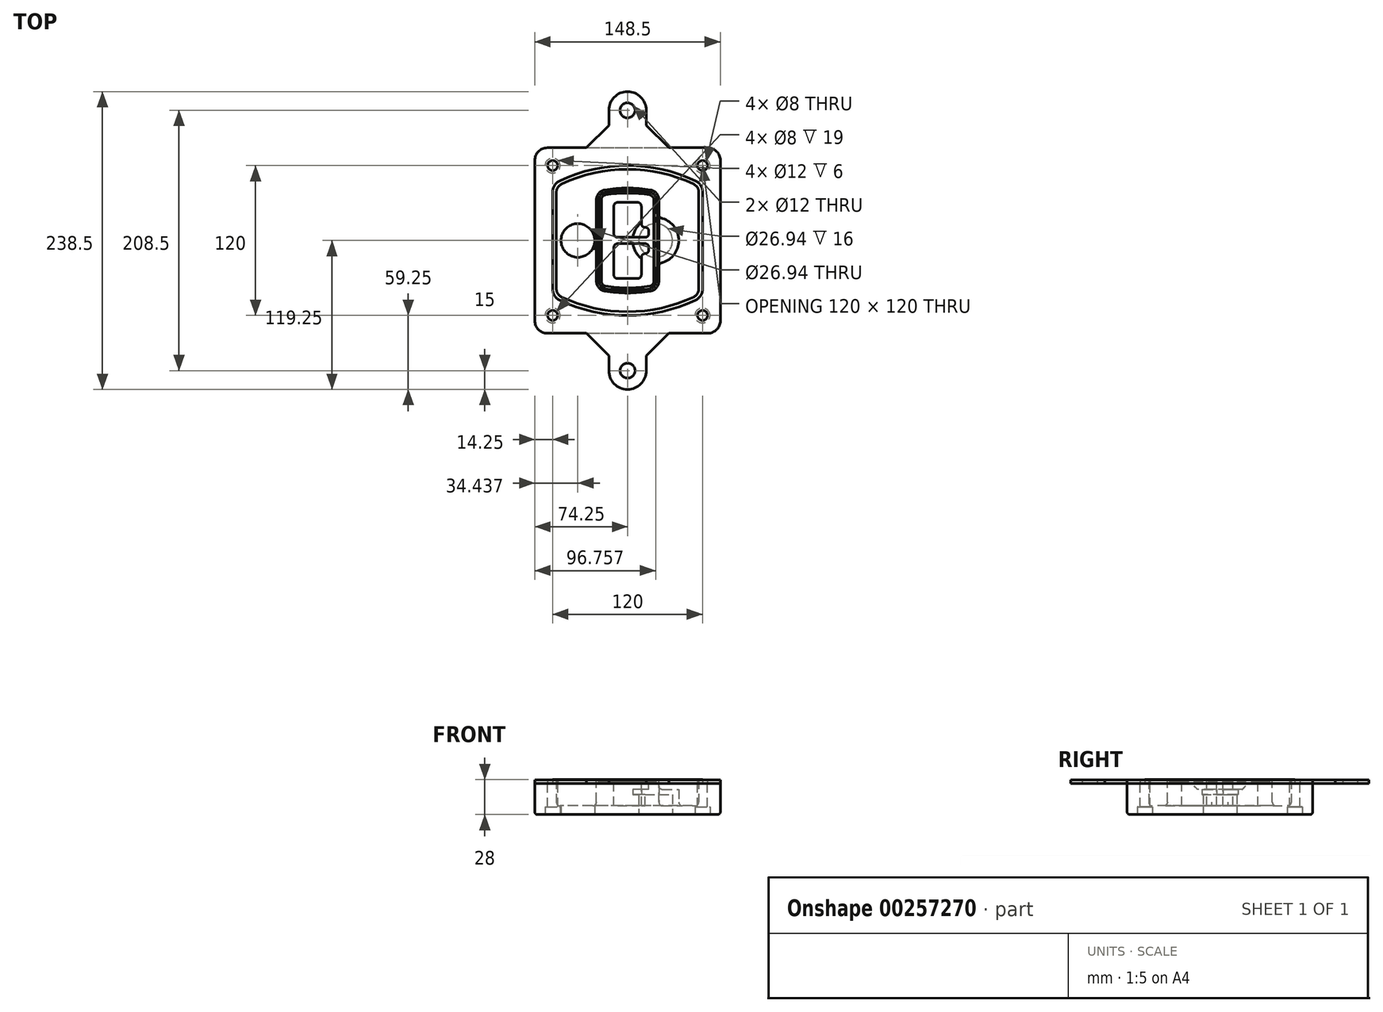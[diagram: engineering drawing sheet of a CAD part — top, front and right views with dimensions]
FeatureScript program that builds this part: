
annotation { "Feature Type Name" : "Feature", "Feature Type Description" : "" }
export const myFeature = defineFeature(function(context is Context, id is Id, definition is map)
    precondition{}
    {
        {
            var Q0;
            Q0=qCreatedBy(makeId("Top.planeOp"),FACE);
            var sketch = newSketch(context, id + "F0", { "sketchPlane" : qUnion([Q0])});
            skPoint(sketch, "E0.rect.middle", {"position": v(0, 0) * mm});
            skLineSegment(sketch, "E1.bottom", {"start": v(-64.25, -74.25) * mm, "end": v(64.25, -74.25) * mm});
            skLineSegment(sketch, "E1.top", {"start": v(-64.25, 74.25) * mm, "end": v(64.25, 74.25) * mm});
            skLineSegment(sketch, "E1.left", {"start": v(-74.25, -64.25) * mm, "end": v(-74.25, 64.25) * mm});
            skLineSegment(sketch, "E1.right", {"start": v(74.25, -64.25) * mm, "end": v(74.25, 64.25) * mm});
            skLineSegment(sketch, "E2", {"start": v(-74.25, 74.25) * mm, "end": v(74.25, -74.25) * mm, "construction": true});
            skLineSegment(sketch, "E3", {"start": v(74.25, 74.25) * mm, "end": v(-74.25, -74.25) * mm, "construction": true});
            skCircle(sketch, "E4", {"center": v(-60, 60) * mm, "radius": 4 * mm});
            skCircle(sketch, "E5", {"center": v(60, 60) * mm, "radius": 4 * mm});
            skCircle(sketch, "E6", {"center": v(60, -60) * mm, "radius": 4 * mm});
            skCircle(sketch, "E7", {"center": v(-60, -60) * mm, "radius": 4 * mm});
            skLineSegment(sketch, "E8", {"start": v(-60, 60) * mm, "end": v(60, 60) * mm, "construction": true});
            skLineSegment(sketch, "E9", {"start": v(60, 60) * mm, "end": v(60, -60) * mm, "construction": true});
            skLineSegment(sketch, "E10", {"start": v(60, -60) * mm, "end": v(-60, -60) * mm, "construction": true});
            skLineSegment(sketch, "E11", {"start": v(-60, -60) * mm, "end": v(-60, 60) * mm, "construction": true});
            skLineSegment(sketch, "E12", {"start": v(-60, 38.83) * mm, "end": v(-60, -38.83) * mm});
            skLineSegment(sketch, "E13", {"start": v(60, 38.83) * mm, "end": v(60, -38.83) * mm});
            skArc(sketch, "E14", {"start": v(54.26, 47.88) * mm, "mid": v(0, 60) * mm, "end": v(-54.26, 47.88) * mm});
            skArc(sketch, "E15", {"start": v(-54.26, -47.88) * mm, "mid": v(0, -60) * mm, "end": v(54.26, -47.88) * mm});
            skLineSegment(sketch, "E16", {"start": v(-60, 0) * mm, "end": v(60, 0) * mm, "construction": true});
            skPoint(sketch, "E17.visualSharp", {"position": v(-60, -45) * mm});
            skArc(sketch, "E17.filletArc", {"start": v(-60, -38.83) * mm, "mid": v(-58.44, -44.2) * mm, "end": v(-54.26, -47.88) * mm});
            skPoint(sketch, "E18.visualSharp", {"position": v(-60, 45) * mm});
            skArc(sketch, "E18.filletArc", {"start": v(-54.26, 47.88) * mm, "mid": v(-58.44, 44.2) * mm, "end": v(-60, 38.83) * mm});
            skPoint(sketch, "E19.visualSharp", {"position": v(60, 45) * mm});
            skArc(sketch, "E19.filletArc", {"start": v(60, 38.83) * mm, "mid": v(58.44, 44.2) * mm, "end": v(54.26, 47.88) * mm});
            skPoint(sketch, "E20.visualSharp", {"position": v(60, -45) * mm});
            skArc(sketch, "E20.filletArc", {"start": v(54.26, -47.88) * mm, "mid": v(58.44, -44.2) * mm, "end": v(60, -38.83) * mm});
            skPoint(sketch, "E21.visualSharp", {"position": v(-74.25, 74.25) * mm});
            skArc(sketch, "E21.filletArc", {"start": v(-64.25, 74.25) * mm, "mid": v(-71.32, 71.32) * mm, "end": v(-74.25, 64.25) * mm});
            skPoint(sketch, "E22.visualSharp", {"position": v(74.25, 74.25) * mm});
            skArc(sketch, "E22.filletArc", {"start": v(74.25, 64.25) * mm, "mid": v(71.32, 71.32) * mm, "end": v(64.25, 74.25) * mm});
            skPoint(sketch, "E23.visualSharp", {"position": v(74.25, -74.25) * mm});
            skArc(sketch, "E23.filletArc", {"start": v(64.25, -74.25) * mm, "mid": v(71.32, -71.32) * mm, "end": v(74.25, -64.25) * mm});
            skPoint(sketch, "E24.visualSharp", {"position": v(-74.25, -74.25) * mm});
            skArc(sketch, "E24.filletArc", {"start": v(-74.25, -64.25) * mm, "mid": v(-71.32, -71.32) * mm, "end": v(-64.25, -74.25) * mm});
            skArc(sketch, "E25.0", {"start": v(57, 38.83) * mm, "mid": v(55.9, 42.58) * mm, "end": v(52.98, 45.17) * mm});
            skLineSegment(sketch, "E25.1", {"start": v(57, 38.83) * mm, "end": v(57, -38.83) * mm});
            skArc(sketch, "E25.2", {"start": v(52.98, -45.17) * mm, "mid": v(55.9, -42.58) * mm, "end": v(57, -38.83) * mm});
            skArc(sketch, "E25.3", {"start": v(-52.98, -45.17) * mm, "mid": v(0, -57) * mm, "end": v(52.98, -45.17) * mm});
            skArc(sketch, "E25.4", {"start": v(-57, -38.83) * mm, "mid": v(-55.9, -42.58) * mm, "end": v(-52.98, -45.17) * mm});
            skArc(sketch, "E25.5", {"start": v(52.98, 45.17) * mm, "mid": v(0, 57) * mm, "end": v(-52.98, 45.17) * mm});
            skLineSegment(sketch, "E25.6", {"start": v(-57, 38.83) * mm, "end": v(-57, -38.83) * mm});
            skArc(sketch, "E25.7", {"start": v(-52.98, 45.17) * mm, "mid": v(-55.9, 42.58) * mm, "end": v(-57, 38.83) * mm});
            skArc(sketch, "E26.0", {"start": v(-55.96, 51.5) * mm, "mid": v(-61.82, 46.33) * mm, "end": v(-64, 38.83) * mm});
            skArc(sketch, "E26.1", {"start": v(55.96, 51.5) * mm, "mid": v(0, 64) * mm, "end": v(-55.96, 51.5) * mm});
            skArc(sketch, "E26.2", {"start": v(64, 38.83) * mm, "mid": v(61.82, 46.33) * mm, "end": v(55.96, 51.5) * mm});
            skLineSegment(sketch, "E26.3", {"start": v(64, 38.83) * mm, "end": v(64, -38.83) * mm});
            skArc(sketch, "E26.4", {"start": v(55.96, -51.5) * mm, "mid": v(61.82, -46.33) * mm, "end": v(64, -38.83) * mm});
            skLineSegment(sketch, "E26.5", {"start": v(-64, 38.83) * mm, "end": v(-64, -38.83) * mm});
            skArc(sketch, "E26.6", {"start": v(-55.96, -51.5) * mm, "mid": v(0, -64) * mm, "end": v(55.96, -51.5) * mm});
            skArc(sketch, "E26.7", {"start": v(-64, -38.83) * mm, "mid": v(-61.82, -46.33) * mm, "end": v(-55.96, -51.5) * mm});
            skSolve(sketch);
        }
        {
            var Q0;
            Q0=makeQuery(id+"F0.imprint","IMPRINT",FACE,{"disambiguationData":[TD([[makeQuery(id+"F0.imprint","IMPRINT",EDGE,{"derivedFrom":sQuery(id+"F0.wireOp",EDGE,"E1.bottom")}),1.0]])]});
            var Q1;
            Q1=makeQuery(id+"F0.imprint","IMPRINT",FACE,{"disambiguationData":[TD([[makeQuery(id+"F0.imprint","IMPRINT",EDGE,{"derivedFrom":sQuery(id+"F0.wireOp",EDGE,"E12")}),1.0]])]});
            var Q2;
            Q2=makeQuery(id+"F0.imprint","IMPRINT",FACE,{"disambiguationData":[TD([[makeQuery(id+"F0.imprint","IMPRINT",EDGE,{"derivedFrom":sQuery(id+"F0.wireOp",EDGE,"E25.0")}),1.0]])]});
            var Q3;
            Q3=makeQuery(id+"F0.imprint","IMPRINT",FACE,{"disambiguationData":[TD([[makeQuery(id+"F0.imprint","IMPRINT",EDGE,{"derivedFrom":sQuery(id+"F0.wireOp",EDGE,"E12")}),-1.0]])]});
            extrude(context, id + "F1", {"entities" : qUnion([Q0, Q1, Q2, Q3]), "oppositeDirection" : true, "depth" : 25 * mm});
        }
        {
            var Q0;
            Q0=makeQuery(id+"F0.imprint","IMPRINT",FACE,{"disambiguationData":[TD([[makeQuery(id+"F0.imprint","IMPRINT",EDGE,{"derivedFrom":sQuery(id+"F0.wireOp",EDGE,"E12")}),1.0]])]});
            extrude(context, id + "F2", {"entities" : qUnion([Q0]), "operationType" : NewBodyOperationType.ADD, "depth" : 3 * mm});
        }
        {
            var Q0;
            Q0=makeQuery(id+"F0.imprint","IMPRINT",FACE,{"disambiguationData":[TD([[makeQuery(id+"F0.imprint","IMPRINT",EDGE,{"derivedFrom":sQuery(id+"F0.wireOp",EDGE,"E25.0")}),1.0]])]});
            extrude(context, id + "F3", {"entities" : qUnion([Q0]), "operationType" : NewBodyOperationType.REMOVE, "oppositeDirection" : true, "depth" : 18 * mm});
        }
        {
            var Q0;
            Q0=makeQuery(id+"F2.opExtrude","CAP_FACE",FACE,{"disambiguationData":[OSD([sQuery(id+"F0.wireOp",EDGE,"E12"),sQuery(id+"F0.wireOp",EDGE,"E13"),sQuery(id+"F0.wireOp",EDGE,"E14"),sQuery(id+"F0.wireOp",EDGE,"E15"),sQuery(id+"F0.wireOp",EDGE,"E17.filletArc"),sQuery(id+"F0.wireOp",EDGE,"E18.filletArc"),sQuery(id+"F0.wireOp",EDGE,"E19.filletArc"),sQuery(id+"F0.wireOp",EDGE,"E20.filletArc"),sQuery(id+"F0.wireOp",EDGE,"E25.0"),sQuery(id+"F0.wireOp",EDGE,"E25.1"),sQuery(id+"F0.wireOp",EDGE,"E25.2"),sQuery(id+"F0.wireOp",EDGE,"E25.3"),sQuery(id+"F0.wireOp",EDGE,"E25.4"),sQuery(id+"F0.wireOp",EDGE,"E25.5"),sQuery(id+"F0.wireOp",EDGE,"E25.6"),sQuery(id+"F0.wireOp",EDGE,"E25.7")])],"isStart":false});
            var sketch = newSketch(context, id + "F4", { "sketchPlane" : qUnion([Q0])});
            skArc(sketch, "E27.0", {"start": v(-18.34, -40.45) * mm, "mid": v(0, -42) * mm, "end": v(18.34, -40.45) * mm});
            skArc(sketch, "E28.0", {"start": v(18.34, 40.45) * mm, "mid": v(0, 42) * mm, "end": v(-18.34, 40.45) * mm});
            skLineSegment(sketch, "E29", {"start": v(-25, 32.57) * mm, "end": v(-25, -32.57) * mm});
            skLineSegment(sketch, "E30", {"start": v(25, 32.57) * mm, "end": v(25, -32.57) * mm});
            skLineSegment(sketch, "E31", {"start": v(-25, 39.1) * mm, "end": v(25, 39.1) * mm, "construction": true});
            skLineSegment(sketch, "E32", {"start": v(-25, -39.1) * mm, "end": v(25, -39.1) * mm, "construction": true});
            skPoint(sketch, "E33.visualSharp", {"position": v(-25, 39.1) * mm});
            skArc(sketch, "E33.filletArc", {"start": v(-18.34, 40.45) * mm, "mid": v(-23.11, 37.73) * mm, "end": v(-25, 32.57) * mm});
            skPoint(sketch, "E34.visualSharp", {"position": v(25, 39.1) * mm});
            skArc(sketch, "E34.filletArc", {"start": v(25, 32.57) * mm, "mid": v(23.11, 37.73) * mm, "end": v(18.34, 40.45) * mm});
            skPoint(sketch, "E35.visualSharp", {"position": v(25, -39.1) * mm});
            skArc(sketch, "E35.filletArc", {"start": v(18.34, -40.45) * mm, "mid": v(23.11, -37.73) * mm, "end": v(25, -32.57) * mm});
            skPoint(sketch, "E36.visualSharp", {"position": v(-25, -39.1) * mm});
            skArc(sketch, "E36.filletArc", {"start": v(-25, -32.57) * mm, "mid": v(-23.11, -37.73) * mm, "end": v(-18.34, -40.45) * mm});
            skArc(sketch, "E37.0", {"start": v(52.98, 45.17) * mm, "mid": v(0, 57) * mm, "end": v(-52.98, 45.17) * mm});
            skArc(sketch, "E37.1", {"start": v(-52.98, 45.17) * mm, "mid": v(-55.9, 42.58) * mm, "end": v(-57, 38.83) * mm});
            skLineSegment(sketch, "E37.2", {"start": v(-57, 38.83) * mm, "end": v(-57, -38.83) * mm});
            skArc(sketch, "E37.3", {"start": v(-57, -38.83) * mm, "mid": v(-55.9, -42.58) * mm, "end": v(-52.98, -45.17) * mm});
            skArc(sketch, "E37.4", {"start": v(-52.98, -45.17) * mm, "mid": v(0, -57) * mm, "end": v(52.98, -45.17) * mm});
            skArc(sketch, "E37.5", {"start": v(52.98, -45.17) * mm, "mid": v(55.9, -42.58) * mm, "end": v(57, -38.83) * mm});
            skLineSegment(sketch, "E37.6", {"start": v(57, 38.83) * mm, "end": v(57, -38.83) * mm});
            skArc(sketch, "E37.7", {"start": v(57, 38.83) * mm, "mid": v(55.9, 42.58) * mm, "end": v(52.98, 45.17) * mm});
            skLineSegment(sketch, "E38.0", {"start": v(23, 32.57) * mm, "end": v(23, -32.57) * mm});
            skArc(sketch, "E38.1", {"start": v(18, -38.48) * mm, "mid": v(21.58, -36.44) * mm, "end": v(23, -32.57) * mm});
            skArc(sketch, "E38.2", {"start": v(-18, -38.48) * mm, "mid": v(0, -40) * mm, "end": v(18, -38.48) * mm});
            skArc(sketch, "E38.3", {"start": v(-23, -32.57) * mm, "mid": v(-21.58, -36.44) * mm, "end": v(-18, -38.48) * mm});
            skLineSegment(sketch, "E38.4", {"start": v(-23, 32.57) * mm, "end": v(-23, -32.57) * mm});
            skArc(sketch, "E38.5", {"start": v(23, 32.57) * mm, "mid": v(21.58, 36.44) * mm, "end": v(18, 38.48) * mm});
            skArc(sketch, "E38.6", {"start": v(-18, 38.48) * mm, "mid": v(-21.58, 36.44) * mm, "end": v(-23, 32.57) * mm});
            skArc(sketch, "E38.7", {"start": v(18, 38.48) * mm, "mid": v(0, 40) * mm, "end": v(-18, 38.48) * mm});
            skArc(sketch, "E39.0", {"start": v(21, 32.57) * mm, "mid": v(20.06, 35.15) * mm, "end": v(17.67, 36.5) * mm});
            skLineSegment(sketch, "E39.1", {"start": v(21, 32.57) * mm, "end": v(21, -32.57) * mm});
            skArc(sketch, "E39.2", {"start": v(17.67, -36.5) * mm, "mid": v(20.06, -35.15) * mm, "end": v(21, -32.57) * mm});
            skArc(sketch, "E39.3", {"start": v(-17.67, -36.5) * mm, "mid": v(0, -38) * mm, "end": v(17.67, -36.5) * mm});
            skArc(sketch, "E39.4", {"start": v(-21, -32.57) * mm, "mid": v(-20.06, -35.15) * mm, "end": v(-17.67, -36.5) * mm});
            skArc(sketch, "E39.5", {"start": v(17.67, 36.5) * mm, "mid": v(0, 38) * mm, "end": v(-17.67, 36.5) * mm});
            skLineSegment(sketch, "E39.6", {"start": v(-21, 32.57) * mm, "end": v(-21, -32.57) * mm});
            skArc(sketch, "E39.7", {"start": v(-17.67, 36.5) * mm, "mid": v(-20.06, 35.15) * mm, "end": v(-21, 32.57) * mm});
            skLineSegment(sketch, "E40", {"start": v(-25, 0) * mm, "end": v(25, 0) * mm, "construction": true});
            skLineSegment(sketch, "E41", {"start": v(-11, 5.5) * mm, "end": v(-11, 27.5) * mm});
            skLineSegment(sketch, "E42", {"start": v(-8, 30.5) * mm, "end": v(8, 30.5) * mm});
            skLineSegment(sketch, "E43", {"start": v(11, 27.5) * mm, "end": v(11, 13.5) * mm});
            skLineSegment(sketch, "E44", {"start": v(14, 10.5) * mm, "end": v(14, 10.5) * mm});
            skLineSegment(sketch, "E45", {"start": v(17, 7.5) * mm, "end": v(17, 5.5) * mm});
            skLineSegment(sketch, "E46", {"start": v(14, 2.5) * mm, "end": v(-8, 2.5) * mm});
            skPoint(sketch, "E47.visualSharp", {"position": v(-11, 30.5) * mm});
            skArc(sketch, "E47.filletArc", {"start": v(-8, 30.5) * mm, "mid": v(-10.12, 29.62) * mm, "end": v(-11, 27.5) * mm});
            skPoint(sketch, "E48.visualSharp", {"position": v(11, 30.5) * mm});
            skArc(sketch, "E48.filletArc", {"start": v(11, 27.5) * mm, "mid": v(10.12, 29.62) * mm, "end": v(8, 30.5) * mm});
            skPoint(sketch, "E49.visualSharp", {"position": v(11, 10.5) * mm});
            skArc(sketch, "E49.filletArc", {"start": v(11, 13.5) * mm, "mid": v(11.88, 11.38) * mm, "end": v(14, 10.5) * mm});
            skPoint(sketch, "E50.visualSharp", {"position": v(17, 10.5) * mm});
            skArc(sketch, "E50.filletArc", {"start": v(17, 7.5) * mm, "mid": v(16.12, 9.62) * mm, "end": v(14, 10.5) * mm});
            skPoint(sketch, "E51.visualSharp", {"position": v(17, 2.5) * mm});
            skArc(sketch, "E51.filletArc", {"start": v(14, 2.5) * mm, "mid": v(16.12, 3.38) * mm, "end": v(17, 5.5) * mm});
            skPoint(sketch, "E52.visualSharp", {"position": v(-11, 2.5) * mm});
            skArc(sketch, "E52.filletArc", {"start": v(-11, 5.5) * mm, "mid": v(-10.12, 3.38) * mm, "end": v(-8, 2.5) * mm});
            skLineSegment(sketch, "E53.0.MirrorCS", {"start": v(14, -2.5) * mm, "end": v(-8, -2.5) * mm});
            skArc(sketch, "E54.0.MirrorCS", {"start": v(-11, -5.5) * mm, "mid": v(-10.12, -3.38) * mm, "end": v(-8, -2.5) * mm});
            skLineSegment(sketch, "E55.0.MirrorCS", {"start": v(-11, -5.5) * mm, "end": v(-11, -27.5) * mm});
            skArc(sketch, "E56.0.MirrorCS", {"start": v(-8, -30.5) * mm, "mid": v(-10.12, -29.62) * mm, "end": v(-11, -27.5) * mm});
            skLineSegment(sketch, "E57.0.MirrorCS", {"start": v(-8, -30.5) * mm, "end": v(8, -30.5) * mm});
            skArc(sketch, "E58.0.MirrorCS", {"start": v(11, -27.5) * mm, "mid": v(10.12, -29.62) * mm, "end": v(8, -30.5) * mm});
            skLineSegment(sketch, "E59.0.MirrorCS", {"start": v(11, -27.5) * mm, "end": v(11, -13.5) * mm});
            skArc(sketch, "E60.0.MirrorCS", {"start": v(11, -13.5) * mm, "mid": v(11.88, -11.38) * mm, "end": v(14, -10.5) * mm});
            skArc(sketch, "E61.0.MirrorCS", {"start": v(17, -7.5) * mm, "mid": v(16.12, -9.62) * mm, "end": v(14, -10.5) * mm});
            skLineSegment(sketch, "E62.0.MirrorCS", {"start": v(17, -7.5) * mm, "end": v(17, -5.5) * mm});
            skArc(sketch, "E63.0.MirrorCS", {"start": v(14, -2.5) * mm, "mid": v(16.12, -3.38) * mm, "end": v(17, -5.5) * mm});
            skSolve(sketch);
        }
        {
            var Q0;
            Q0=makeQuery(id+"F4.imprint","IMPRINT",FACE,{"disambiguationData":[TD([[makeQuery(id+"F4.imprint","IMPRINT",EDGE,{"derivedFrom":sQuery(id+"F4.wireOp",EDGE,"E27.0")}),1.0]])]});
            var Q1;
            Q1=makeQuery(id+"F4.imprint","IMPRINT",FACE,{"disambiguationData":[TD([[makeQuery(id+"F4.imprint","IMPRINT",EDGE,{"derivedFrom":sQuery(id+"F4.wireOp",EDGE,"E38.0")}),-1.0]])]});
            var Q2;
            Q2=makeQuery(id+"F4.imprint","IMPRINT",FACE,{"disambiguationData":[TD([[makeQuery(id+"F4.imprint","IMPRINT",EDGE,{"derivedFrom":sQuery(id+"F4.wireOp",EDGE,"E39.0")}),1.0]])]});
            extrude(context, id + "F5", {"entities" : qUnion([Q0, Q1, Q2]), "operationType" : NewBodyOperationType.ADD, "endBound" : BoundingType.UP_TO_NEXT, "oppositeDirection" : true, "depth" : 25 * mm});
        }
        {
            var Q0;
            Q0=makeQuery(id+"F4.imprint","IMPRINT",FACE,{"disambiguationData":[TD([[makeQuery(id+"F4.imprint","IMPRINT",EDGE,{"derivedFrom":sQuery(id+"F4.wireOp",EDGE,"E38.0")}),-1.0]])]});
            extrude(context, id + "F6", {"entities" : qUnion([Q0]), "operationType" : NewBodyOperationType.REMOVE, "oppositeDirection" : true, "depth" : 2 * mm});
        }
        {
            var Q0;
            Q0=makeQuery(id+"F1.opExtrude","CAP_FACE",FACE,{"disambiguationData":[OSD([sQuery(id+"F0.wireOp",EDGE,"E1.bottom"),sQuery(id+"F0.wireOp",EDGE,"E1.top"),sQuery(id+"F0.wireOp",EDGE,"E1.left"),sQuery(id+"F0.wireOp",EDGE,"E1.right"),sQuery(id+"F0.wireOp",EDGE,"E4"),sQuery(id+"F0.wireOp",EDGE,"E5"),sQuery(id+"F0.wireOp",EDGE,"E6"),sQuery(id+"F0.wireOp",EDGE,"E7"),sQuery(id+"F0.wireOp",EDGE,"E21.filletArc"),sQuery(id+"F0.wireOp",EDGE,"E22.filletArc"),sQuery(id+"F0.wireOp",EDGE,"E23.filletArc"),sQuery(id+"F0.wireOp",EDGE,"E24.filletArc")])],"isStart":false});
            var sketch = newSketch(context, id + "F7", { "sketchPlane" : qUnion([Q0])});
            skCircle(sketch, "E64", {"center": v(22.5, 0) * mm, "radius": 13.47 * mm});
            skCircle(sketch, "E65", {"center": v(-39.81, 0) * mm, "radius": 13.47 * mm});
            skLineSegment(sketch, "E66", {"start": v(74.25, 0) * mm, "end": v(-74.25, 0) * mm});
            skCircle(sketch, "E67", {"center": v(22.5, 0) * mm, "radius": 18.47 * mm});
            skCircle(sketch, "E68", {"center": v(60, -60) * mm, "radius": 6 * mm});
            skCircle(sketch, "E69", {"center": v(-60, -60) * mm, "radius": 6 * mm});
            skCircle(sketch, "E70", {"center": v(-60, 60) * mm, "radius": 6 * mm});
            skCircle(sketch, "E71", {"center": v(60, 60) * mm, "radius": 6 * mm});
            skSolve(sketch);
        }
        {
            var Q0;
            {var subQ1=sQuery(id+"F7.wireOp",EDGE,"E66");var subQ4=sQuery(id+"F7.wireOp",EDGE,"E64");var subQ6=makeQuery(id+"F7.imprint","INTERSECT",VERTEX,{"disambiguationData":[OD(0.0)],"derivedFrom":[subQ4,subQ1]});Q0=makeQuery(id+"F7.imprint","IMPRINT",FACE,{"disambiguationData":[TD([[makeQuery(id+"F7.imprint","IMPRINT",EDGE,{"disambiguationData":[TD([[subQ6,-1.0]])],"derivedFrom":subQ4}),-1.0]])]});}
            var Q1;
            {var subQ0=sQuery(id+"F7.wireOp",EDGE,"E66");var subQ1=sQuery(id+"F7.wireOp",EDGE,"E64");var subQ3=makeQuery(id+"F7.imprint","INTERSECT",VERTEX,{"disambiguationData":[OD(0.0)],"derivedFrom":[subQ1,subQ0]});Q1=makeQuery(id+"F7.imprint","IMPRINT",FACE,{"disambiguationData":[TD([[makeQuery(id+"F7.imprint","IMPRINT",EDGE,{"disambiguationData":[TD([[subQ3,-1.0]])],"derivedFrom":subQ1}),1.0]])]});}
            var Q2;
            {var subQ0=sQuery(id+"F7.wireOp",EDGE,"E66");var subQ1=sQuery(id+"F7.wireOp",EDGE,"E64");var subQ3=makeQuery(id+"F7.imprint","INTERSECT",VERTEX,{"disambiguationData":[OD(0.0)],"derivedFrom":[subQ1,subQ0]});Q2=makeQuery(id+"F7.imprint","IMPRINT",FACE,{"disambiguationData":[TD([[makeQuery(id+"F7.imprint","IMPRINT",EDGE,{"disambiguationData":[TD([[subQ3,1.0]])],"derivedFrom":subQ1}),1.0]])]});}
            var Q3;
            {var subQ1=sQuery(id+"F7.wireOp",EDGE,"E66");var subQ4=sQuery(id+"F7.wireOp",EDGE,"E64");var subQ6=makeQuery(id+"F7.imprint","INTERSECT",VERTEX,{"disambiguationData":[OD(0.0)],"derivedFrom":[subQ4,subQ1]});Q3=makeQuery(id+"F7.imprint","IMPRINT",FACE,{"disambiguationData":[TD([[makeQuery(id+"F7.imprint","IMPRINT",EDGE,{"disambiguationData":[TD([[subQ6,1.0]])],"derivedFrom":subQ4}),-1.0]])]});}
            extrude(context, id + "F8", {"entities" : qUnion([Q0, Q1, Q2, Q3]), "operationType" : NewBodyOperationType.ADD, "oppositeDirection" : true, "depth" : 20 * mm});
        }
        {
            var Q0;
            {var subQ0=sQuery(id+"F7.wireOp",EDGE,"E66");var subQ1=sQuery(id+"F7.wireOp",EDGE,"E64");var subQ3=makeQuery(id+"F7.imprint","INTERSECT",VERTEX,{"disambiguationData":[OD(0.0)],"derivedFrom":[subQ1,subQ0]});Q0=makeQuery(id+"F7.imprint","IMPRINT",FACE,{"disambiguationData":[TD([[makeQuery(id+"F7.imprint","IMPRINT",EDGE,{"disambiguationData":[TD([[subQ3,-1.0]])],"derivedFrom":subQ1}),1.0]])]});}
            var Q1;
            {var subQ0=sQuery(id+"F7.wireOp",EDGE,"E66");var subQ1=sQuery(id+"F7.wireOp",EDGE,"E64");var subQ3=makeQuery(id+"F7.imprint","INTERSECT",VERTEX,{"disambiguationData":[OD(0.0)],"derivedFrom":[subQ1,subQ0]});Q1=makeQuery(id+"F7.imprint","IMPRINT",FACE,{"disambiguationData":[TD([[makeQuery(id+"F7.imprint","IMPRINT",EDGE,{"disambiguationData":[TD([[subQ3,1.0]])],"derivedFrom":subQ1}),1.0]])]});}
            extrude(context, id + "F9", {"entities" : qUnion([Q0, Q1]), "operationType" : NewBodyOperationType.REMOVE, "oppositeDirection" : true, "depth" : 16 * mm});
        }
        {
            var Q0;
            {var subQ0=sQuery(id+"F7.wireOp",EDGE,"E66");var subQ1=sQuery(id+"F7.wireOp",EDGE,"E65");var subQ3=makeQuery(id+"F7.imprint","INTERSECT",VERTEX,{"disambiguationData":[OD(0.0)],"derivedFrom":[subQ1,subQ0]});Q0=makeQuery(id+"F7.imprint","IMPRINT",FACE,{"disambiguationData":[TD([[makeQuery(id+"F7.imprint","IMPRINT",EDGE,{"disambiguationData":[TD([[subQ3,-1.0]])],"derivedFrom":subQ1}),1.0]])]});}
            var Q1;
            {var subQ0=sQuery(id+"F7.wireOp",EDGE,"E66");var subQ1=sQuery(id+"F7.wireOp",EDGE,"E65");var subQ3=makeQuery(id+"F7.imprint","INTERSECT",VERTEX,{"disambiguationData":[OD(0.0)],"derivedFrom":[subQ1,subQ0]});Q1=makeQuery(id+"F7.imprint","IMPRINT",FACE,{"disambiguationData":[TD([[makeQuery(id+"F7.imprint","IMPRINT",EDGE,{"disambiguationData":[TD([[subQ3,1.0]])],"derivedFrom":subQ1}),1.0]])]});}
            extrude(context, id + "F10", {"entities" : qUnion([Q0, Q1]), "operationType" : NewBodyOperationType.REMOVE, "oppositeDirection" : true, "depth" : 25 * mm});
        }
        {
            var Q0;
            Q0=makeQuery(id+"F7.imprint","IMPRINT",FACE,{"disambiguationData":[TD([[makeQuery(id+"F7.imprint","IMPRINT",EDGE,{"derivedFrom":sQuery(id+"F7.wireOp",EDGE,"E68")}),1.0]])]});
            var Q1;
            Q1=makeQuery(id+"F7.imprint","IMPRINT",FACE,{"disambiguationData":[TD([[makeQuery(id+"F7.imprint","IMPRINT",EDGE,{"derivedFrom":makeQuery(id+"F1.opExtrude","CAP_EDGE",EDGE,{"disambiguationData":[OSD([sQuery(id+"F0.wireOp",EDGE,"E5")])],"isStart":false})}),-1.0]])]});
            var Q2;
            Q2=makeQuery(id+"F7.imprint","IMPRINT",FACE,{"disambiguationData":[TD([[makeQuery(id+"F7.imprint","IMPRINT",EDGE,{"derivedFrom":sQuery(id+"F7.wireOp",EDGE,"E69")}),1.0]])]});
            var Q3;
            Q3=makeQuery(id+"F7.imprint","IMPRINT",FACE,{"disambiguationData":[TD([[makeQuery(id+"F7.imprint","IMPRINT",EDGE,{"derivedFrom":makeQuery(id+"F1.opExtrude","CAP_EDGE",EDGE,{"disambiguationData":[OSD([sQuery(id+"F0.wireOp",EDGE,"E4")])],"isStart":false})}),-1.0]])]});
            var Q4;
            Q4=makeQuery(id+"F7.imprint","IMPRINT",FACE,{"disambiguationData":[TD([[makeQuery(id+"F7.imprint","IMPRINT",EDGE,{"derivedFrom":sQuery(id+"F7.wireOp",EDGE,"E70")}),1.0]])]});
            var Q5;
            Q5=makeQuery(id+"F7.imprint","IMPRINT",FACE,{"disambiguationData":[TD([[makeQuery(id+"F7.imprint","IMPRINT",EDGE,{"derivedFrom":makeQuery(id+"F1.opExtrude","CAP_EDGE",EDGE,{"disambiguationData":[OSD([sQuery(id+"F0.wireOp",EDGE,"E7")])],"isStart":false})}),-1.0]])]});
            var Q6;
            Q6=makeQuery(id+"F7.imprint","IMPRINT",FACE,{"disambiguationData":[TD([[makeQuery(id+"F7.imprint","IMPRINT",EDGE,{"derivedFrom":sQuery(id+"F7.wireOp",EDGE,"E71")}),1.0]])]});
            var Q7;
            Q7=makeQuery(id+"F7.imprint","IMPRINT",FACE,{"disambiguationData":[TD([[makeQuery(id+"F7.imprint","IMPRINT",EDGE,{"derivedFrom":makeQuery(id+"F1.opExtrude","CAP_EDGE",EDGE,{"disambiguationData":[OSD([sQuery(id+"F0.wireOp",EDGE,"E6")])],"isStart":false})}),-1.0]])]});
            extrude(context, id + "F11", {"entities" : qUnion([Q0, Q1, Q2, Q3, Q4, Q5, Q6, Q7]), "operationType" : NewBodyOperationType.REMOVE, "oppositeDirection" : true, "depth" : 6 * mm});
        }
        {
            var Q0;
            Q0=makeQuery(id+"F9.boolean.opBoolean","COPY",FACE,{"derivedFrom":makeQuery(id+"F9.opExtrude","CAP_FACE",FACE,{"disambiguationData":[OSD([sQuery(id+"F7.wireOp",EDGE,"E64")])],"isStart":false})});
            var sketch = newSketch(context, id + "F12", { "sketchPlane" : qUnion([Q0])});
            skArc(sketch, "E72.0", {"start": v(11, 14.45) * mm, "mid": v(6.45, 9.13) * mm, "end": v(4.2, 2.5) * mm});
            skArc(sketch, "E72.1", {"start": v(4.2, -2.5) * mm, "mid": v(6.45, -9.13) * mm, "end": v(11, -14.45) * mm});
            skLineSegment(sketch, "E73", {"start": v(4.2, -2.5) * mm, "end": v(14, -2.5) * mm});
            skLineSegment(sketch, "E74.0", {"start": v(14, 2.5) * mm, "end": v(4.2, 2.5) * mm});
            skArc(sketch, "E74.1", {"start": v(14, 2.5) * mm, "mid": v(16.12, 3.38) * mm, "end": v(17, 5.5) * mm});
            skLineSegment(sketch, "E74.2", {"start": v(17, 7.5) * mm, "end": v(17, 5.5) * mm});
            skArc(sketch, "E74.3", {"start": v(17, 7.5) * mm, "mid": v(16.12, 9.62) * mm, "end": v(14, 10.5) * mm});
            skArc(sketch, "E74.4", {"start": v(11, 13.5) * mm, "mid": v(11.88, 11.38) * mm, "end": v(14, 10.5) * mm});
            skLineSegment(sketch, "E74.5", {"start": v(11, 14.45) * mm, "end": v(11, 13.5) * mm});
            skLineSegment(sketch, "E74.7", {"start": v(14, -2.5) * mm, "end": v(4.2, -2.5) * mm});
            skArc(sketch, "E74.8", {"start": v(14, -2.5) * mm, "mid": v(16.12, -3.38) * mm, "end": v(17, -5.5) * mm});
            skLineSegment(sketch, "E74.9", {"start": v(17, -7.5) * mm, "end": v(17, -5.5) * mm});
            skArc(sketch, "E74.10", {"start": v(17, -7.5) * mm, "mid": v(16.12, -9.62) * mm, "end": v(14, -10.5) * mm});
            skArc(sketch, "E74.11", {"start": v(11, -13.5) * mm, "mid": v(11.88, -11.38) * mm, "end": v(14, -10.5) * mm});
            skLineSegment(sketch, "E74.12", {"start": v(11, -14.45) * mm, "end": v(11, -13.5) * mm});
            skPoint(sketch, "E75.orphan", {"position": v(11, -27.5) * mm});
            skPoint(sketch, "E76.orphan", {"position": v(-8, -2.5) * mm});
            skPoint(sketch, "E77.orphan", {"position": v(-8, 2.5) * mm});
            skPoint(sketch, "E78.orphan", {"position": v(11, 27.5) * mm});
            skSolve(sketch);
        }
        {
            var Q0;
            {var subQ7=sQuery(id+"F12.wireOp",EDGE,"E72.0");var subQ14=sQuery(id+"F12.wireOp",EDGE,"E72.1");var subQ16=sQuery(id+"F12.wireOp",EDGE,"E74.1");var subQ18=sQuery(id+"F12.wireOp",EDGE,"E74.8");Q0=qUnion([makeQuery(id+"F12.imprint","IMPRINT",FACE,{"disambiguationData":[TD([[makeQuery(id+"F12.imprint","IMPRINT",EDGE,{"derivedFrom":subQ7}),1.0]])]}),makeQuery(id+"F12.imprint","IMPRINT",FACE,{"disambiguationData":[TD([[makeQuery(id+"F12.imprint","IMPRINT",EDGE,{"derivedFrom":subQ14}),1.0]])]}),makeQuery(id+"F12.imprint","IMPRINT",FACE,{"disambiguationData":[TD([[makeQuery(id+"F12.imprint","IMPRINT",EDGE,{"derivedFrom":subQ16}),1.0]])]}),makeQuery(id+"F12.imprint","IMPRINT",FACE,{"disambiguationData":[TD([[makeQuery(id+"F12.imprint","IMPRINT",EDGE,{"derivedFrom":subQ18}),-1.0]])]})]);}
            var Q1;
            Q1=makeQuery(id+"F5.boolean.opBoolean","SPLIT",FACE,{"disambiguationData":[TD([makeQuery(id+"F5.opExtrude","SWEPT_FACE",FACE,{"disambiguationData":[OSD([sQuery(id+"F4.wireOp",EDGE,"E41")])]})])],"derivedFrom":makeQuery(id+"F3.boolean.opBoolean","COPY",FACE,{"derivedFrom":makeQuery(id+"F3.opExtrude","CAP_FACE",FACE,{"disambiguationData":[OSD([sQuery(id+"F0.wireOp",EDGE,"E25.0"),sQuery(id+"F0.wireOp",EDGE,"E25.1"),sQuery(id+"F0.wireOp",EDGE,"E25.2"),sQuery(id+"F0.wireOp",EDGE,"E25.3"),sQuery(id+"F0.wireOp",EDGE,"E25.4"),sQuery(id+"F0.wireOp",EDGE,"E25.5"),sQuery(id+"F0.wireOp",EDGE,"E25.6"),sQuery(id+"F0.wireOp",EDGE,"E25.7")])],"isStart":false})})});
            extrude(context, id + "F13", {"entities" : qUnion([Q0]), "operationType" : NewBodyOperationType.REMOVE, "endBound" : BoundingType.UP_TO_SURFACE, "endBoundEntityFace" : qUnion([Q1]), "depth" : 25 * mm});
        }
        {
            var Q0;
            Q0=makeQuery(id+"F3.boolean.opBoolean","COPY",EDGE,{"derivedFrom":makeQuery(id+"F3.opExtrude","CAP_EDGE",EDGE,{"disambiguationData":[OSD([sQuery(id+"F0.wireOp",EDGE,"E25.6")])],"isStart":false})});
            var Q1;
            Q1=makeQuery(id+"F8.boolean.opBoolean","INTERSECT",EDGE,{"derivedFrom":[makeQuery(id+"F5.opExtrude","SWEPT_FACE",FACE,{"disambiguationData":[OSD([sQuery(id+"F4.wireOp",EDGE,"E30")])]}),makeQuery(id+"F8.opExtrude","CAP_FACE",FACE,{"disambiguationData":[OSD([sQuery(id+"F7.wireOp",EDGE,"E67")])],"isStart":false})]});
            var Q2;
            Q2=makeQuery(id+"F8.boolean.opBoolean","INTERSECT",EDGE,{"disambiguationData":[OD(1.0)],"derivedFrom":[makeQuery(id+"F5.opExtrude","SWEPT_FACE",FACE,{"disambiguationData":[OSD([sQuery(id+"F4.wireOp",EDGE,"E30")])]}),makeQuery(id+"F8.opExtrude","SWEPT_FACE",FACE,{"disambiguationData":[OSD([sQuery(id+"F7.wireOp",EDGE,"E67")])]})]});
            var Q3;
            {var subQ0=sQuery(id+"F4.wireOp",EDGE,"E30");Q3=makeQuery(id+"F8.boolean.opBoolean","SPLIT",EDGE,{"disambiguationData":[TD([makeQuery(id+"F5.opExtrude","SWEPT_FACE",FACE,{"disambiguationData":[OSD([sQuery(id+"F4.wireOp",EDGE,"E35.filletArc")])]})])],"derivedFrom":makeQuery(id+"F5.opExtrude","CAP_EDGE",EDGE,{"disambiguationData":[OSD([subQ0])],"isStart":false})});}
            var Q4;
            {var subQ0=sQuery(id+"F0.wireOp",EDGE,"E25.7");var subQ1=sQuery(id+"F0.wireOp",EDGE,"E25.1");var subQ2=sQuery(id+"F0.wireOp",EDGE,"E25.6");var subQ3=sQuery(id+"F0.wireOp",EDGE,"E25.5");var subQ4=sQuery(id+"F0.wireOp",EDGE,"E25.4");var subQ5=sQuery(id+"F0.wireOp",EDGE,"E25.0");var subQ6=sQuery(id+"F0.wireOp",EDGE,"E25.2");var subQ7=sQuery(id+"F0.wireOp",EDGE,"E25.3");Q4=makeQuery(id+"F8.boolean.opBoolean","INTERSECT",EDGE,{"derivedFrom":[makeQuery(id+"F5.boolean.opBoolean","SPLIT",FACE,{"disambiguationData":[TD([makeQuery(id+"F2.opExtrude","SWEPT_FACE",FACE,{"disambiguationData":[OSD([subQ5])]})])],"derivedFrom":makeQuery(id+"F3.boolean.opBoolean","COPY",FACE,{"derivedFrom":makeQuery(id+"F3.opExtrude","CAP_FACE",FACE,{"disambiguationData":[OSD([subQ5,subQ1,subQ6,subQ7,subQ4,subQ3,subQ2,subQ0])],"isStart":false})})}),makeQuery(id+"F8.opExtrude","SWEPT_FACE",FACE,{"disambiguationData":[OSD([sQuery(id+"F7.wireOp",EDGE,"E67")])]})]});}
            var Q5;
            Q5=makeQuery(id+"F8.boolean.opBoolean","INTERSECT",EDGE,{"disambiguationData":[OD(0.0)],"derivedFrom":[makeQuery(id+"F5.opExtrude","SWEPT_FACE",FACE,{"disambiguationData":[OSD([sQuery(id+"F4.wireOp",EDGE,"E30")])]}),makeQuery(id+"F8.opExtrude","SWEPT_FACE",FACE,{"disambiguationData":[OSD([sQuery(id+"F7.wireOp",EDGE,"E67")])]})]});
            fillet(context, id + "F14", {"entities" : qUnion([Q0, Q1, Q2, Q3, Q4, Q5]), "radius" : 3 * mm, "tangentPropagation" : true, "allowEdgeOverflow" : false});
        }
        {
            var Q0;
            Q0=makeQuery(id+"F1.opExtrude","CAP_EDGE",EDGE,{"disambiguationData":[OSD([sQuery(id+"F0.wireOp",EDGE,"E1.bottom")])],"isStart":false});
            fillet(context, id + "F15", {"entities" : qUnion([Q0]), "radius" : 2 * mm, "tangentPropagation" : true, "allowEdgeOverflow" : false});
        }
        {
            var Q0;
            {var subQ0=sQuery(id+"F0.wireOp",EDGE,"E22.filletArc");var subQ1=sQuery(id+"F0.wireOp",EDGE,"E7");var subQ2=sQuery(id+"F0.wireOp",EDGE,"E6");var subQ3=sQuery(id+"F0.wireOp",EDGE,"E5");var subQ4=sQuery(id+"F0.wireOp",EDGE,"E4");var subQ5=sQuery(id+"F0.wireOp",EDGE,"E1.bottom");var subQ6=sQuery(id+"F0.wireOp",EDGE,"E21.filletArc");var subQ7=sQuery(id+"F0.wireOp",EDGE,"E1.top");var subQ8=sQuery(id+"F0.wireOp",EDGE,"E1.left");var subQ9=sQuery(id+"F0.wireOp",EDGE,"E1.right");var subQ10=sQuery(id+"F0.wireOp",EDGE,"E23.filletArc");var subQ11=sQuery(id+"F0.wireOp",EDGE,"E24.filletArc");Q0=makeQuery(id+"F2.boolean.opBoolean","SPLIT",FACE,{"disambiguationData":[TD([makeQuery(id+"F1.opExtrude","SWEPT_FACE",FACE,{"disambiguationData":[OSD([subQ5])]})])],"derivedFrom":makeQuery(id+"F1.opExtrude","CAP_FACE",FACE,{"disambiguationData":[OSD([subQ5,subQ7,subQ8,subQ9,subQ4,subQ3,subQ2,subQ1,subQ6,subQ0,subQ10,subQ11])],"isStart":true})});}
            var sketch = newSketch(context, id + "F16", { "sketchPlane" : qUnion([Q0])});
            skLineSegment(sketch, "E79", {"start": v(0, 74.25) * mm, "end": v(0, 104.25) * mm, "construction": true});
            skCircle(sketch, "E80", {"center": v(0, 104.25) * mm, "radius": 6 * mm});
            skLineSegment(sketch, "E81", {"start": v(-33, 74.25) * mm, "end": v(-15, 92.25) * mm});
            skLineSegment(sketch, "E82", {"start": v(-15, 92.25) * mm, "end": v(-15, 104.25) * mm});
            skArc(sketch, "E83", {"start": v(15, 104.25) * mm, "mid": v(0, 119.25) * mm, "end": v(-15, 104.25) * mm});
            skLineSegment(sketch, "E84", {"start": v(15, 104.25) * mm, "end": v(15, 92.25) * mm});
            skLineSegment(sketch, "E85", {"start": v(15, 92.25) * mm, "end": v(33, 74.25) * mm});
            skLineSegment(sketch, "E86", {"start": v(-74.25, 0) * mm, "end": v(74.25, 0) * mm, "construction": true});
            skPoint(sketch, "E86.startSnap0", {"position": v(-74.25, 0) * mm});
            skPoint(sketch, "E86.endSnap0", {"position": v(74.25, 0) * mm});
            skLineSegment(sketch, "E87.MirrorCS", {"start": v(-33, -74.25) * mm, "end": v(-15, -92.25) * mm});
            skLineSegment(sketch, "E88.MirrorCS", {"start": v(-15, -92.25) * mm, "end": v(-15, -104.25) * mm});
            skArc(sketch, "E89.MirrorCS", {"start": v(15, -104.25) * mm, "mid": v(0, -119.25) * mm, "end": v(-15, -104.25) * mm});
            skCircle(sketch, "E90.MirrorC", {"center": v(0, -104.25) * mm, "radius": 6 * mm});
            skLineSegment(sketch, "E91.MirrorCS", {"start": v(15, -104.25) * mm, "end": v(15, -92.25) * mm});
            skLineSegment(sketch, "E92.MirrorCS", {"start": v(15, -92.25) * mm, "end": v(33, -74.25) * mm});
            skLineSegment(sketch, "E93.MirrorCS", {"start": v(0, -74.25) * mm, "end": v(0, -104.25) * mm, "construction": true});
            skSolve(sketch);
        }
        {
            var Q0;
            Q0=makeQuery(id+"F16.imprint","IMPRINT",FACE,{"disambiguationData":[TD([[makeQuery(id+"F16.imprint","IMPRINT",EDGE,{"derivedFrom":sQuery(id+"F16.wireOp",EDGE,"E80")}),-1.0]])]});
            var Q1;
            {var subQ0=sQuery(id+"F16.wireOp",EDGE,"E87.MirrorCS");Q1=makeQuery(id+"F16.imprint","IMPRINT",FACE,{"disambiguationData":[TD([[makeQuery(id+"F16.imprint","IMPRINT",EDGE,{"derivedFrom":subQ0}),1.0]])]});}
            var Q2;
            Q2=makeQuery(id+"F16.imprint","IMPRINT",FACE,{"disambiguationData":[TD([[makeQuery(id+"F16.imprint","IMPRINT",EDGE,{"derivedFrom":makeQuery(id+"F1.opExtrude","CAP_EDGE",EDGE,{"disambiguationData":[OSD([sQuery(id+"F0.wireOp",EDGE,"E1.left")])],"isStart":true})}),-1.0]])]});
            extrude(context, id + "F17", {"entities" : qUnion([Q0, Q1, Q2]), "depth" : 2.8 * mm});
        }
    });
